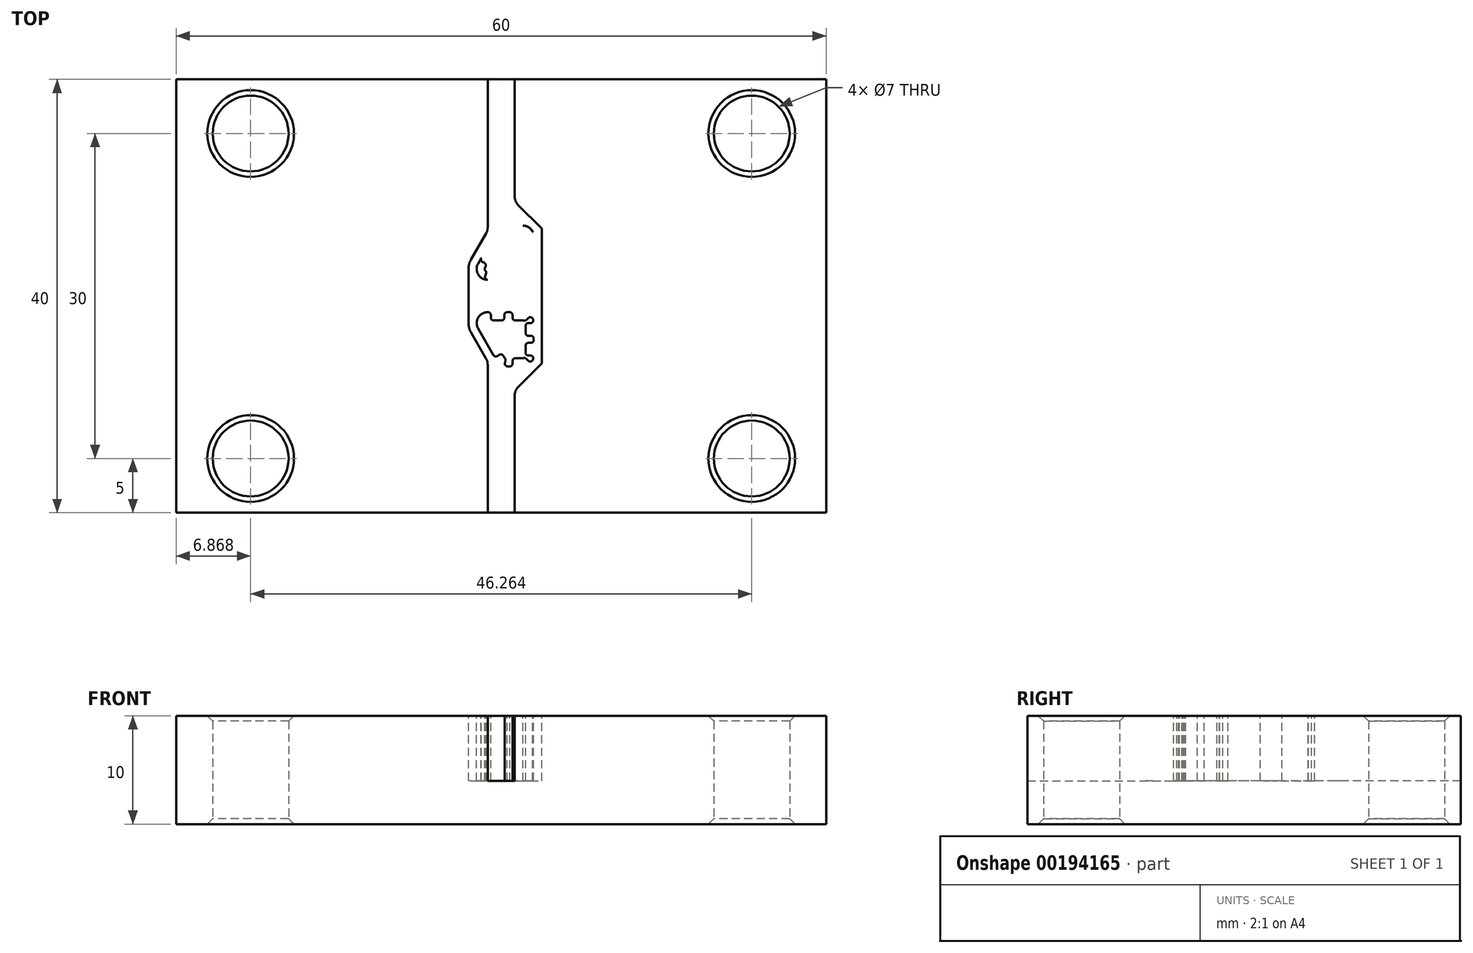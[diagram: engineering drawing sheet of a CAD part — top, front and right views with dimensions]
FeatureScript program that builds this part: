
annotation { "Feature Type Name" : "Feature", "Feature Type Description" : "" }
export const myFeature = defineFeature(function(context is Context, id is Id, definition is map)
    precondition{}
    {
        {
            var Q0;
            Q0=qCreatedBy(makeId("Top.planeOp"),FACE);
            var sketch = newSketch(context, id + "F0", { "sketchPlane" : qUnion([Q0])});
            skLineSegment(sketch, "E0.bottom", {"start": v(-30, 20) * mm, "end": v(30, 20) * mm});
            skLineSegment(sketch, "E0.top", {"start": v(-30, -20) * mm, "end": v(30, -20) * mm});
            skLineSegment(sketch, "E0.left", {"start": v(-30, 20) * mm, "end": v(-30, -20) * mm});
            skLineSegment(sketch, "E0.right", {"start": v(30, 20) * mm, "end": v(30, -20) * mm});
            skLineSegment(sketch, "E1", {"start": v(0, 99.86) * mm, "end": v(0, -61.69) * mm, "construction": true});
            skLineSegment(sketch, "E2", {"start": v(-65.53, 0) * mm, "end": v(113.19, 0) * mm, "construction": true});
            skLineSegment(sketch, "E3", {"start": v(-23.13, 86.06) * mm, "end": v(-23.13, -88.18) * mm, "construction": true});
            skLineSegment(sketch, "E4", {"start": v(23.13, 86.8) * mm, "end": v(23.13, -92.66) * mm, "construction": true});
            skLineSegment(sketch, "E5", {"start": v(-43.06, 15) * mm, "end": v(51.45, 15) * mm, "construction": true});
            skLineSegment(sketch, "E6", {"start": v(-43.93, -15) * mm, "end": v(58.43, -15) * mm, "construction": true});
            skCircle(sketch, "E7", {"center": v(-23.13, 15) * mm, "radius": 3.5 * mm});
            skCircle(sketch, "E8.MirrorC", {"center": v(23.13, 15) * mm, "radius": 3.5 * mm});
            skCircle(sketch, "E9.MirrorC", {"center": v(23.13, -15) * mm, "radius": 3.5 * mm});
            skCircle(sketch, "E10.MirrorC", {"center": v(-23.13, -15) * mm, "radius": 3.5 * mm});
            skSolve(sketch);
        }
        {
            var Q0;
            Q0=makeQuery(id+"F0.imprint","IMPRINT",FACE,{"disambiguationData":[TD([[makeQuery(id+"F0.imprint","IMPRINT",EDGE,{"derivedFrom":sQuery(id+"F0.wireOp",EDGE,"E0.bottom")}),-1.0]])]});
            extrude(context, id + "F1", {"entities" : qUnion([Q0]), "depth" : 10 * mm});
        }
        {
            var Q0;
            Q0=makeQuery(id+"F1.opExtrude","SWEPT_FACE",FACE,{"disambiguationData":[OSD([sQuery(id+"F0.wireOp",EDGE,"E7")])]});
            var Q1;
            Q1=makeQuery(id+"F1.opExtrude","SWEPT_FACE",FACE,{"disambiguationData":[OSD([sQuery(id+"F0.wireOp",EDGE,"E10.MirrorC")])]});
            var Q2;
            Q2=makeQuery(id+"F1.opExtrude","SWEPT_FACE",FACE,{"disambiguationData":[OSD([sQuery(id+"F0.wireOp",EDGE,"E9.MirrorC")])]});
            var Q3;
            Q3=makeQuery(id+"F1.opExtrude","SWEPT_FACE",FACE,{"disambiguationData":[OSD([sQuery(id+"F0.wireOp",EDGE,"E8.MirrorC")])]});
            chamfer(context, id + "F2", {"entities" : qUnion([Q0, Q1, Q2, Q3]), "width" : 0.5 * mm, "tangentPropagation" : true});
        }
        {
            var Q0;
            Q0=makeQuery(id+"F1.opExtrude","CAP_FACE",FACE,{"disambiguationData":[OSD([sQuery(id+"F0.wireOp",EDGE,"E0.bottom"),sQuery(id+"F0.wireOp",EDGE,"E0.top"),sQuery(id+"F0.wireOp",EDGE,"E0.left"),sQuery(id+"F0.wireOp",EDGE,"E0.right"),sQuery(id+"F0.wireOp",EDGE,"E7"),sQuery(id+"F0.wireOp",EDGE,"E8.MirrorC"),sQuery(id+"F0.wireOp",EDGE,"E9.MirrorC"),sQuery(id+"F0.wireOp",EDGE,"E10.MirrorC")])],"isStart":false});
            var sketch = newSketch(context, id + "F3", { "sketchPlane" : qUnion([Q0])});
            skLineSegment(sketch, "E11", {"start": v(0, 60.75) * mm, "end": v(0, -62.05) * mm, "construction": true});
            skLineSegment(sketch, "E12", {"start": v(-90.4, 0) * mm, "end": v(109.57, 0) * mm, "construction": true});
            skLineSegment(sketch, "E13", {"start": v(-1.27, 1.5) * mm, "end": v(2, 1.5) * mm});
            skLineSegment(sketch, "E14", {"start": v(3, 3.92) * mm, "end": v(3, 4.07) * mm});
            skLineSegment(sketch, "E15", {"start": v(2, 6.5) * mm, "end": v(0.46, 6.5) * mm});
            skLineSegment(sketch, "E16", {"start": v(-0.4, 6) * mm, "end": v(-2.13, 3) * mm});
            skArc(sketch, "E17", {"start": v(2.94, 5.83) * mm, "mid": v(2.58, 6.32) * mm, "end": v(2, 6.5) * mm});
            skArc(sketch, "E18", {"start": v(-2.13, 3) * mm, "mid": v(-2.13, 2) * mm, "end": v(-1.27, 1.5) * mm});
            skArc(sketch, "E19", {"start": v(0.46, 6.5) * mm, "mid": v(-0.04, 6.37) * mm, "end": v(-0.4, 6) * mm});
            skPoint(sketch, "E20.orphan", {"position": v(-3, 1.5) * mm});
            skLineSegment(sketch, "E21.trimOffspring", {"start": v(0, 6.5) * mm, "end": v(-0.11, 6.5) * mm});
            skLineSegment(sketch, "E22", {"start": v(2.7, 5.5) * mm, "end": v(2.5, 5.5) * mm});
            skLineSegment(sketch, "E23", {"start": v(2.25, 5.25) * mm, "end": v(2.25, 4.57) * mm});
            skLineSegment(sketch, "E24", {"start": v(2.5, 4.32) * mm, "end": v(2.75, 4.32) * mm});
            skArc(sketch, "E25", {"start": v(2.5, 5.5) * mm, "mid": v(2.32, 5.43) * mm, "end": v(2.25, 5.25) * mm});
            skLineSegment(sketch, "E26", {"start": v(2.17, 4.91) * mm, "end": v(3.34, 4.91) * mm, "construction": true});
            skPoint(sketch, "E26.startSnap0", {"position": v(2.25, 4.91) * mm});
            skArc(sketch, "E27.MirrorC", {"start": v(2.5, 4.32) * mm, "mid": v(2.32, 4.4) * mm, "end": v(2.25, 4.57) * mm});
            skArc(sketch, "E28", {"start": v(3, 4.07) * mm, "mid": v(2.93, 4.25) * mm, "end": v(2.75, 4.32) * mm});
            skArc(sketch, "E29", {"start": v(2.7, 5.5) * mm, "mid": v(2.91, 5.6) * mm, "end": v(2.94, 5.83) * mm});
            skPoint(sketch, "E30.orphan", {"position": v(3, 4.32) * mm});
            skPoint(sketch, "E31.orphan", {"position": v(3, 5.5) * mm});
            skPoint(sketch, "E32.orphan", {"position": v(2.25, 5.5) * mm});
            skPoint(sketch, "E33.orphan", {"position": v(2.25, 4.32) * mm});
            skLineSegment(sketch, "E34", {"start": v(1.75, 4) * mm, "end": v(4.02, 4) * mm, "construction": true});
            skArc(sketch, "E35.MirrorCS", {"start": v(2.7, 2.5) * mm, "mid": v(2.91, 2.4) * mm, "end": v(2.94, 2.17) * mm});
            skArc(sketch, "E36.MirrorCS", {"start": v(3, 3.92) * mm, "mid": v(2.93, 3.75) * mm, "end": v(2.75, 3.67) * mm});
            skArc(sketch, "E37.MirrorCS", {"start": v(2.5, 3.67) * mm, "mid": v(2.32, 3.6) * mm, "end": v(2.25, 3.42) * mm});
            skLineSegment(sketch, "E38.MirrorCS", {"start": v(2.5, 3.67) * mm, "end": v(2.75, 3.67) * mm});
            skPoint(sketch, "E39.MirrorP", {"position": v(2.25, 3.67) * mm});
            skArc(sketch, "E40.MirrorCS", {"start": v(2.5, 2.5) * mm, "mid": v(2.32, 2.57) * mm, "end": v(2.25, 2.75) * mm});
            skPoint(sketch, "E41.MirrorP", {"position": v(2.25, 3.09) * mm});
            skPoint(sketch, "E42.MirrorP", {"position": v(3, 3.67) * mm});
            skLineSegment(sketch, "E43.MirrorCS", {"start": v(2.25, 2.75) * mm, "end": v(2.25, 3.42) * mm});
            skLineSegment(sketch, "E44.MirrorCS", {"start": v(2.7, 2.5) * mm, "end": v(2.5, 2.5) * mm});
            skPoint(sketch, "E45.MirrorP", {"position": v(2.25, 2.5) * mm});
            skPoint(sketch, "E46.MirrorP", {"position": v(3, 2.5) * mm});
            skPoint(sketch, "E47.orphan", {"position": v(3, 8) * mm});
            skLineSegment(sketch, "E48", {"start": v(3.75, 20) * mm, "end": v(3.75, -20) * mm});
            skLineSegment(sketch, "E49", {"start": v(-3.02, 20) * mm, "end": v(-3.02, -20) * mm});
            skLineSegment(sketch, "E50", {"start": v(-1.25, 20) * mm, "end": v(-1.25, 6.3) * mm});
            skLineSegment(sketch, "E51", {"start": v(1.25, 20) * mm, "end": v(1.25, 9.14) * mm});
            skLineSegment(sketch, "E52", {"start": v(-2.78, 3.37) * mm, "end": v(-1.38, 5.8) * mm});
            skArc(sketch, "E53.trimOffspring", {"start": v(-2.78, 3.37) * mm, "mid": v(-2.96, 2.95) * mm, "end": v(-3.02, 2.5) * mm});
            skArc(sketch, "E54", {"start": v(-1.38, 5.8) * mm, "mid": v(-1.28, 6.04) * mm, "end": v(-1.25, 6.3) * mm});
            skLineSegment(sketch, "E55", {"start": v(1.54, 8.43) * mm, "end": v(3.75, 6.22) * mm});
            skArc(sketch, "E56", {"start": v(1.25, 9.14) * mm, "mid": v(1.33, 8.76) * mm, "end": v(1.54, 8.43) * mm});
            skCircle(sketch, "E57", {"center": v(2, 2.5) * mm, "radius": 1 * mm, "construction": true});
            skLineSegment(sketch, "E58", {"start": v(3, 6.49) * mm, "end": v(3, 1.28) * mm, "construction": true});
            skArc(sketch, "E59", {"start": v(2, 1.5) * mm, "mid": v(2.58, 1.68) * mm, "end": v(2.94, 2.17) * mm});
            skArc(sketch, "E60.MirrorCS", {"start": v(2.7, -5.5) * mm, "mid": v(2.91, -5.6) * mm, "end": v(2.94, -5.83) * mm});
            skLineSegment(sketch, "E61.MirrorCS", {"start": v(2.7, -5.5) * mm, "end": v(2.5, -5.5) * mm});
            skArc(sketch, "E62.MirrorCS", {"start": v(2.5, -5.5) * mm, "mid": v(2.32, -5.43) * mm, "end": v(2.25, -5.25) * mm});
            skArc(sketch, "E63.MirrorCS", {"start": v(3, -3.92) * mm, "mid": v(2.93, -3.75) * mm, "end": v(2.75, -3.67) * mm});
            skLineSegment(sketch, "E64.MirrorCS", {"start": v(2.5, -4.32) * mm, "end": v(2.75, -4.32) * mm});
            skLineSegment(sketch, "E65.MirrorCS", {"start": v(2.25, -5.25) * mm, "end": v(2.25, -4.57) * mm});
            skLineSegment(sketch, "E66.MirrorCS", {"start": v(3, -3.92) * mm, "end": v(3, -4.07) * mm});
            skArc(sketch, "E67.MirrorCS", {"start": v(2.5, -4.32) * mm, "mid": v(2.32, -4.4) * mm, "end": v(2.25, -4.57) * mm});
            skLineSegment(sketch, "E68.MirrorCS", {"start": v(2.17, -4.91) * mm, "end": v(3.34, -4.91) * mm, "construction": true});
            skArc(sketch, "E69.MirrorCS", {"start": v(3, -4.07) * mm, "mid": v(2.93, -4.25) * mm, "end": v(2.75, -4.32) * mm});
            skLineSegment(sketch, "E70.MirrorCS", {"start": v(2.5, -3.67) * mm, "end": v(2.75, -3.67) * mm});
            skArc(sketch, "E71.MirrorCS", {"start": v(2.5, -3.67) * mm, "mid": v(2.32, -3.6) * mm, "end": v(2.25, -3.42) * mm});
            skLineSegment(sketch, "E72.MirrorCS", {"start": v(2.7, -2.5) * mm, "end": v(2.5, -2.5) * mm});
            skLineSegment(sketch, "E73.MirrorCS", {"start": v(2.25, -2.75) * mm, "end": v(2.25, -3.42) * mm});
            skArc(sketch, "E74.MirrorCS", {"start": v(2.5, -2.5) * mm, "mid": v(2.32, -2.57) * mm, "end": v(2.25, -2.75) * mm});
            skArc(sketch, "E75.MirrorCS", {"start": v(2.7, -2.5) * mm, "mid": v(2.91, -2.4) * mm, "end": v(2.94, -2.17) * mm});
            skLineSegment(sketch, "E76.MirrorCS", {"start": v(0, -6.5) * mm, "end": v(-0.11, -6.5) * mm});
            skArc(sketch, "E77.MirrorCS", {"start": v(2.94, -5.83) * mm, "mid": v(2.58, -6.32) * mm, "end": v(2, -6.5) * mm});
            skArc(sketch, "E78.MirrorCS", {"start": v(1.25, -9.14) * mm, "mid": v(1.33, -8.76) * mm, "end": v(1.54, -8.43) * mm});
            skArc(sketch, "E79.MirrorCS", {"start": v(0.46, -6.5) * mm, "mid": v(-0.04, -6.37) * mm, "end": v(-0.4, -6) * mm});
            skLineSegment(sketch, "E80.MirrorCS", {"start": v(2, -6.5) * mm, "end": v(0.46, -6.5) * mm});
            skArc(sketch, "E81.MirrorCS", {"start": v(-1.38, -5.8) * mm, "mid": v(-1.28, -6.04) * mm, "end": v(-1.25, -6.3) * mm});
            skLineSegment(sketch, "E82.MirrorCS", {"start": v(3, -6.49) * mm, "end": v(3, -1.28) * mm, "construction": true});
            skLineSegment(sketch, "E83.MirrorCS", {"start": v(1.75, -4) * mm, "end": v(4.02, -4) * mm, "construction": true});
            skArc(sketch, "E84.MirrorCS", {"start": v(2, -1.5) * mm, "mid": v(2.58, -1.68) * mm, "end": v(2.94, -2.17) * mm});
            skPoint(sketch, "E85.MirrorP", {"position": v(3, -4.32) * mm});
            skPoint(sketch, "E86.MirrorP", {"position": v(2.25, -3.67) * mm});
            skLineSegment(sketch, "E87.MirrorCS", {"start": v(1.54, -8.43) * mm, "end": v(3.75, -6.22) * mm});
            skPoint(sketch, "E88.MirrorP", {"position": v(2.25, -4.32) * mm});
            skPoint(sketch, "E89.MirrorP", {"position": v(2.25, -4.91) * mm});
            skPoint(sketch, "E90.MirrorP", {"position": v(2.25, -5.5) * mm});
            skArc(sketch, "E91.MirrorCS", {"start": v(-2.78, -3.37) * mm, "mid": v(-2.96, -2.95) * mm, "end": v(-3.02, -2.5) * mm});
            skPoint(sketch, "E92.MirrorP", {"position": v(3, -5.5) * mm});
            skPoint(sketch, "E93.MirrorP", {"position": v(3, -3.67) * mm});
            skPoint(sketch, "E94.MirrorP", {"position": v(2.25, -3.09) * mm});
            skArc(sketch, "E95.MirrorCS", {"start": v(-2.13, -3) * mm, "mid": v(-2.13, -2) * mm, "end": v(-1.27, -1.5) * mm});
            skPoint(sketch, "E96.MirrorP", {"position": v(3, -2.5) * mm});
            skLineSegment(sketch, "E97.MirrorCS", {"start": v(-0.4, -6) * mm, "end": v(-2.13, -3) * mm});
            skLineSegment(sketch, "E98.MirrorCS", {"start": v(-1.27, -1.5) * mm, "end": v(2, -1.5) * mm});
            skPoint(sketch, "E99.MirrorP", {"position": v(2.25, -2.5) * mm});
            skPoint(sketch, "E100.MirrorP", {"position": v(-3, -1.5) * mm});
            skLineSegment(sketch, "E101.MirrorCS", {"start": v(-2.78, -3.37) * mm, "end": v(-1.38, -5.8) * mm});
            skLineSegment(sketch, "E102.MirrorCS", {"start": v(1.25, -20) * mm, "end": v(1.25, -9.14) * mm});
            skPoint(sketch, "E103.MirrorP", {"position": v(3, -8) * mm});
            skLineSegment(sketch, "E104.MirrorCS", {"start": v(-1.25, -20) * mm, "end": v(-1.25, -6.3) * mm});
            skCircle(sketch, "E105.MirrorC", {"center": v(2, -2.5) * mm, "radius": 1 * mm, "construction": true});
            skSolve(sketch);
        }
        {
            var Q0;
            Q0=makeQuery(id+"F3.imprint","IMPRINT",FACE,{"disambiguationData":[TD([[makeQuery(id+"F3.imprint","IMPRINT",EDGE,{"derivedFrom":sQuery(id+"F3.wireOp",EDGE,"E13")}),-1.0]])]});
            extrude(context, id + "F4", {"entities" : qUnion([Q0]), "operationType" : NewBodyOperationType.REMOVE, "oppositeDirection" : true, "depth" : 6 * mm});
        }
        {
            var Q0;
            Q0=makeQuery(id+"F4.boolean.opBoolean","SPLIT",FACE,{"disambiguationData":[TD([makeQuery(id+"F4.opExtrude","SWEPT_FACE",FACE,{"disambiguationData":[OSD([sQuery(id+"F3.wireOp",EDGE,"E13")])]})])],"derivedFrom":makeQuery(id+"F1.opExtrude","CAP_FACE",FACE,{"disambiguationData":[OSD([sQuery(id+"F0.wireOp",EDGE,"E0.bottom"),sQuery(id+"F0.wireOp",EDGE,"E0.top"),sQuery(id+"F0.wireOp",EDGE,"E0.left"),sQuery(id+"F0.wireOp",EDGE,"E0.right"),sQuery(id+"F0.wireOp",EDGE,"E7"),sQuery(id+"F0.wireOp",EDGE,"E8.MirrorC"),sQuery(id+"F0.wireOp",EDGE,"E9.MirrorC"),sQuery(id+"F0.wireOp",EDGE,"E10.MirrorC")])],"isStart":false})});
            var sketch = newSketch(context, id + "F5", { "sketchPlane" : qUnion([Q0])});
            skLineSegment(sketch, "E106", {"start": v(2.25, 5.48) * mm, "end": v(2.25, 2.5) * mm, "construction": true});
            skPoint(sketch, "E106.startSnap0", {"position": v(2.25, 4.91) * mm});
            skPoint(sketch, "E107.startSnap0", {"position": v(2.91, 2.4) * mm});
            skLineSegment(sketch, "E108", {"start": v(-1.48, 2.62) * mm, "end": v(0.25, 5.62) * mm, "construction": true});
            skLineSegment(sketch, "E109", {"start": v(0.46, 5.75) * mm, "end": v(1.98, 5.75) * mm, "construction": true});
            skLineSegment(sketch, "E110", {"start": v(-1.27, 2.25) * mm, "end": v(2, 2.25) * mm, "construction": true});
            skPoint(sketch, "E111.orphan", {"position": v(2.25, 6.5) * mm});
            skArc(sketch, "E112", {"start": v(-1.48, 2.62) * mm, "mid": v(-1.48, 2.37) * mm, "end": v(-1.27, 2.25) * mm, "construction": true});
            skArc(sketch, "E113", {"start": v(0.46, 5.75) * mm, "mid": v(0.34, 5.72) * mm, "end": v(0.25, 5.62) * mm, "construction": true});
            skArc(sketch, "E114", {"start": v(2.25, 5.48) * mm, "mid": v(2.17, 5.67) * mm, "end": v(1.98, 5.75) * mm, "construction": true});
            skArc(sketch, "E115", {"start": v(2, 2.25) * mm, "mid": v(2.18, 2.32) * mm, "end": v(2.25, 2.5) * mm, "construction": true});
            skPoint(sketch, "E116.orphan", {"position": v(2.7, 6.2) * mm});
            skPoint(sketch, "E117.orphan", {"position": v(-0.04, 6.37) * mm});
            skLineSegment(sketch, "E118", {"start": v(3.45, 5.5) * mm, "end": v(1.72, 5.5) * mm, "construction": true});
            skLineSegment(sketch, "E119", {"start": v(2, 6.65) * mm, "end": v(2, 5.2) * mm, "construction": true});
            skArc(sketch, "E120", {"start": v(2, 6.5) * mm, "mid": v(2.7, 6.2) * mm, "end": v(3, 5.5) * mm});
            skLineSegment(sketch, "E121", {"start": v(2, 5.5) * mm, "end": v(2.88, 6.32) * mm, "construction": true});
            skArc(sketch, "E122", {"start": v(2.92, 5.9) * mm, "mid": v(2.74, 6.04) * mm, "end": v(2.52, 5.98) * mm});
            skArc(sketch, "E123", {"start": v(2.07, 5.74) * mm, "mid": v(2.2, 5.73) * mm, "end": v(2.31, 5.8) * mm});
            skArc(sketch, "E124", {"start": v(1.04, 6) * mm, "mid": v(1.11, 5.82) * mm, "end": v(1.3, 5.75) * mm});
            skArc(sketch, "E125", {"start": v(1.04, 6.25) * mm, "mid": v(0.97, 6.43) * mm, "end": v(0.8, 6.5) * mm});
            skLineSegment(sketch, "E126", {"start": v(1.04, 6.25) * mm, "end": v(1.04, 6) * mm});
            skLineSegment(sketch, "E127.trimOffspring", {"start": v(1.04, 6.25) * mm, "end": v(1.04, 6) * mm, "construction": true});
            skLineSegment(sketch, "E128", {"start": v(2, 2.5) * mm, "end": v(3.17, 1.41) * mm, "construction": true});
            skArc(sketch, "E129", {"start": v(2.52, 2.02) * mm, "mid": v(2.74, 1.96) * mm, "end": v(2.92, 2.1) * mm});
            skArc(sketch, "E130", {"start": v(2.32, 2.2) * mm, "mid": v(2.2, 2.27) * mm, "end": v(2.07, 2.26) * mm});
            skLineSegment(sketch, "E131", {"start": v(2.48, 1.97) * mm, "end": v(2.52, 2.02) * mm, "construction": true});
            skLineSegment(sketch, "E132", {"start": v(2.32, 2.2) * mm, "end": v(2.52, 2.02) * mm});
            skLineSegment(sketch, "E133", {"start": v(1.04, 2.32) * mm, "end": v(1.04, 1.29) * mm, "construction": true});
            skLineSegment(sketch, "E134", {"start": v(2, 2.25) * mm, "end": v(2, 1.38) * mm, "construction": true});
            skArc(sketch, "E135", {"start": v(1.3, 2.25) * mm, "mid": v(1.11, 2.18) * mm, "end": v(1.04, 2) * mm});
            skArc(sketch, "E136", {"start": v(0.8, 1.5) * mm, "mid": v(0.97, 1.57) * mm, "end": v(1.04, 1.75) * mm});
            skLineSegment(sketch, "E137", {"start": v(1.3, 2.25) * mm, "end": v(2, 2.25) * mm});
            skArc(sketch, "E138", {"start": v(2.07, 2.26) * mm, "mid": v(2.04, 2.25) * mm, "end": v(2, 2.25) * mm});
            skLineSegment(sketch, "E139", {"start": v(0.8, 1.75) * mm, "end": v(1.08, 1.75) * mm, "construction": true});
            skLineSegment(sketch, "E140", {"start": v(0.8, 2.02) * mm, "end": v(0.8, 1.42) * mm, "construction": true});
            skLineSegment(sketch, "E141", {"start": v(1.04, 2) * mm, "end": v(1.04, 1.75) * mm});
            skLineSegment(sketch, "E142", {"start": v(0.3, 2) * mm, "end": v(0.3, 1.75) * mm});
            skArc(sketch, "E143", {"start": v(0.3, 1.75) * mm, "mid": v(0.36, 1.57) * mm, "end": v(0.54, 1.5) * mm});
            skArc(sketch, "E144", {"start": v(0.3, 2) * mm, "mid": v(0.22, 2.18) * mm, "end": v(0.04, 2.25) * mm});
            skPoint(sketch, "E145.orphan", {"position": v(0.5, 1.75) * mm});
            skLineSegment(sketch, "E146", {"start": v(0.54, 1.77) * mm, "end": v(0.54, 1.46) * mm, "construction": true});
            skLineSegment(sketch, "E147", {"start": v(-0.96, 2.45) * mm, "end": v(-0.96, 1.28) * mm, "construction": true});
            skLineSegment(sketch, "E148", {"start": v(-0.96, 2) * mm, "end": v(-0.96, 1.75) * mm});
            skLineSegment(sketch, "E149", {"start": v(-0.33, 2.42) * mm, "end": v(-0.33, 1.38) * mm, "construction": true});
            skArc(sketch, "E150.MirrorCS", {"start": v(-0.96, 2) * mm, "mid": v(-0.89, 2.18) * mm, "end": v(-0.7, 2.25) * mm});
            skArc(sketch, "E151.MirrorCS", {"start": v(-0.96, 1.75) * mm, "mid": v(-1.03, 1.57) * mm, "end": v(-1.2, 1.5) * mm});
            skLineSegment(sketch, "E152", {"start": v(-0.7, 2.25) * mm, "end": v(0.04, 2.25) * mm});
            skLineSegment(sketch, "E153", {"start": v(0.46, 5.75) * mm, "end": v(0.46, 6.64) * mm, "construction": true});
            skLineSegment(sketch, "E154", {"start": v(0.46, 5.5) * mm, "end": v(0.23, 6.83) * mm, "construction": true});
            skArc(sketch, "E155", {"start": v(0.59, 6.5) * mm, "mid": v(0.4, 6.41) * mm, "end": v(0.34, 6.2) * mm});
            skArc(sketch, "E156", {"start": v(0.3, 5.7) * mm, "mid": v(0.38, 5.8) * mm, "end": v(0.39, 5.93) * mm});
            skLineSegment(sketch, "E157", {"start": v(0.59, 6.2) * mm, "end": v(0.59, 6.67) * mm, "construction": true});
            skLineSegment(sketch, "E158", {"start": v(0.39, 5.93) * mm, "end": v(0.34, 6.2) * mm});
            skLineSegment(sketch, "E159", {"start": v(0.33, 5.58) * mm, "end": v(-0.79, 6.22) * mm, "construction": true});
            skLineSegment(sketch, "E160", {"start": v(-0.38, 5.55) * mm, "end": v(-0.16, 5.42) * mm});
            skArc(sketch, "E161", {"start": v(-0.16, 5.42) * mm, "mid": v(0.03, 5.4) * mm, "end": v(0.18, 5.51) * mm});
            skArc(sketch, "E162", {"start": v(-0.38, 5.55) * mm, "mid": v(-0.57, 5.57) * mm, "end": v(-0.72, 5.45) * mm});
            skLineSegment(sketch, "E163.trimOffspring", {"start": v(0.06, 5.3) * mm, "end": v(0.33, 5.14) * mm});
            skLineSegment(sketch, "E164", {"start": v(-0.82, 5.51) * mm, "end": v(-0.5, 5.33) * mm, "construction": true});
            skLineSegment(sketch, "E165", {"start": v(-0.5, 5.33) * mm, "end": v(-0.38, 5.55) * mm, "construction": true});
            skLineSegment(sketch, "E166", {"start": v(-0.75, 4.9) * mm, "end": v(-0.53, 4.77) * mm});
            skArc(sketch, "E167", {"start": v(-0.84, 5.24) * mm, "mid": v(-0.87, 5.05) * mm, "end": v(-0.75, 4.9) * mm});
            skArc(sketch, "E168", {"start": v(-0.44, 4.43) * mm, "mid": v(-0.42, 4.62) * mm, "end": v(-0.53, 4.77) * mm});
            skLineSegment(sketch, "E169", {"start": v(-0.63, 5.11) * mm, "end": v(-0.9, 5.28) * mm, "construction": true});
            skLineSegment(sketch, "E170", {"start": v(-0.63, 4.1) * mm, "end": v(-1.44, 4.57) * mm, "construction": true});
            skArc(sketch, "E171.MirrorCS", {"start": v(-0.82, 3.78) * mm, "mid": v(-0.97, 3.66) * mm, "end": v(-1.16, 3.69) * mm});
            skLineSegment(sketch, "E172.MirrorCS", {"start": v(-1.38, 3.81) * mm, "end": v(-1.16, 3.69) * mm});
            skArc(sketch, "E173.MirrorCS", {"start": v(-1.72, 3.72) * mm, "mid": v(-1.57, 3.84) * mm, "end": v(-1.38, 3.81) * mm});
            skArc(sketch, "E174.MirrorCS", {"start": v(-1.75, 3.16) * mm, "mid": v(-1.87, 3.32) * mm, "end": v(-1.84, 3.5) * mm});
            skLineSegment(sketch, "E175.MirrorCS", {"start": v(-1.75, 3.16) * mm, "end": v(-1.53, 3.04) * mm});
            skArc(sketch, "E176.MirrorCS", {"start": v(-1.53, 3.04) * mm, "mid": v(-1.42, 2.89) * mm, "end": v(-1.44, 2.7) * mm});
            skLineSegment(sketch, "E177", {"start": v(-1.84, 3.5) * mm, "end": v(-1.72, 3.72) * mm});
            skLineSegment(sketch, "E178", {"start": v(-0.84, 5.24) * mm, "end": v(-0.72, 5.45) * mm});
            skLineSegment(sketch, "E179", {"start": v(0.18, 5.51) * mm, "end": v(0.25, 5.62) * mm});
            skLineSegment(sketch, "E180", {"start": v(-0.82, 3.78) * mm, "end": v(-0.44, 4.43) * mm});
            skArc(sketch, "E181", {"start": v(0.25, 5.62) * mm, "mid": v(0.27, 5.66) * mm, "end": v(0.3, 5.7) * mm});
            skLineSegment(sketch, "E182", {"start": v(-1.27, 2.5) * mm, "end": v(-1.62, 1.4) * mm, "construction": true});
            skArc(sketch, "E183", {"start": v(-1.49, 1.83) * mm, "mid": v(-1.45, 1.6) * mm, "end": v(-1.25, 1.5) * mm});
            skArc(sketch, "E184", {"start": v(-1.4, 2.09) * mm, "mid": v(-1.4, 2.22) * mm, "end": v(-1.45, 2.33) * mm});
            skLineSegment(sketch, "E185", {"start": v(-1.25, 1.5) * mm, "end": v(-1.2, 1.5) * mm});
            skLineSegment(sketch, "E186", {"start": v(-1.49, 1.83) * mm, "end": v(-1.4, 2.09) * mm});
            skArc(sketch, "E187", {"start": v(-1.45, 2.33) * mm, "mid": v(-1.52, 2.47) * mm, "end": v(-1.48, 2.62) * mm});
            skLineSegment(sketch, "E188", {"start": v(-1.48, 2.62) * mm, "end": v(-1.44, 2.7) * mm});
            skLineSegment(sketch, "E189", {"start": v(1.3, 5.75) * mm, "end": v(1.98, 5.75) * mm});
            skArc(sketch, "E190", {"start": v(1.98, 5.75) * mm, "mid": v(2.03, 5.75) * mm, "end": v(2.07, 5.74) * mm});
            skLineSegment(sketch, "E191", {"start": v(-5.65, 0) * mm, "end": v(4.56, 0) * mm, "construction": true});
            skArc(sketch, "E192", {"start": v(-2.13, 3) * mm, "mid": v(-2.13, 2) * mm, "end": v(-1.27, 1.5) * mm});
            skLineSegment(sketch, "E193", {"start": v(-2.13, 3) * mm, "end": v(-0.4, 6) * mm});
            skArc(sketch, "E194", {"start": v(-0.4, 6) * mm, "mid": v(-0.04, 6.37) * mm, "end": v(0.46, 6.5) * mm});
            skLineSegment(sketch, "E195", {"start": v(0.46, 6.5) * mm, "end": v(2, 6.5) * mm});
            skArc(sketch, "E196", {"start": v(2, 6.5) * mm, "mid": v(2.55, 6.33) * mm, "end": v(2.92, 5.89) * mm});
            skLineSegment(sketch, "E197", {"start": v(-1.25, 1.5) * mm, "end": v(2, 1.5) * mm});
            skArc(sketch, "E198", {"start": v(2, 1.5) * mm, "mid": v(2.55, 1.66) * mm, "end": v(2.92, 2.1) * mm});
            skLineSegment(sketch, "E199", {"start": v(2.31, 5.8) * mm, "end": v(2.52, 5.98) * mm});
            skArc(sketch, "E200.MirrorCS", {"start": v(2.07, -2.26) * mm, "mid": v(2.04, -2.25) * mm, "end": v(2, -2.25) * mm});
            skArc(sketch, "E201.MirrorCS", {"start": v(1.98, -5.75) * mm, "mid": v(2.03, -5.75) * mm, "end": v(2.07, -5.74) * mm});
            skArc(sketch, "E202.MirrorCS", {"start": v(2.25, -5.48) * mm, "mid": v(2.17, -5.67) * mm, "end": v(1.98, -5.75) * mm, "construction": true});
            skArc(sketch, "E203.MirrorCS", {"start": v(2, -2.25) * mm, "mid": v(2.18, -2.32) * mm, "end": v(2.25, -2.5) * mm, "construction": true});
            skArc(sketch, "E204.MirrorCS", {"start": v(2.32, -2.2) * mm, "mid": v(2.2, -2.27) * mm, "end": v(2.07, -2.26) * mm});
            skArc(sketch, "E205.MirrorCS", {"start": v(2.07, -5.74) * mm, "mid": v(2.2, -5.73) * mm, "end": v(2.31, -5.8) * mm});
            skArc(sketch, "E206.MirrorCS", {"start": v(0.25, -5.62) * mm, "mid": v(0.27, -5.66) * mm, "end": v(0.3, -5.7) * mm});
            skLineSegment(sketch, "E207.MirrorCS", {"start": v(-0.96, -2) * mm, "end": v(-0.96, -1.75) * mm});
            skArc(sketch, "E208.MirrorCS", {"start": v(-0.96, -1.75) * mm, "mid": v(-1.03, -1.57) * mm, "end": v(-1.2, -1.5) * mm});
            skArc(sketch, "E209.MirrorCS", {"start": v(-1.49, -1.83) * mm, "mid": v(-1.45, -1.6) * mm, "end": v(-1.25, -1.5) * mm});
            skLineSegment(sketch, "E210.MirrorCS", {"start": v(-1.25, -1.5) * mm, "end": v(-1.2, -1.5) * mm});
            skArc(sketch, "E211.MirrorCS", {"start": v(-1.45, -2.33) * mm, "mid": v(-1.52, -2.47) * mm, "end": v(-1.48, -2.62) * mm});
            skArc(sketch, "E212.MirrorCS", {"start": v(-1.48, -2.62) * mm, "mid": v(-1.48, -2.37) * mm, "end": v(-1.27, -2.25) * mm, "construction": true});
            skArc(sketch, "E213.MirrorCS", {"start": v(0.46, -5.75) * mm, "mid": v(0.34, -5.72) * mm, "end": v(0.25, -5.62) * mm, "construction": true});
            skArc(sketch, "E214.MirrorCS", {"start": v(-0.96, -2) * mm, "mid": v(-0.89, -2.18) * mm, "end": v(-0.7, -2.25) * mm});
            skLineSegment(sketch, "E215.MirrorCS", {"start": v(2.32, -2.2) * mm, "end": v(2.52, -2.02) * mm});
            skArc(sketch, "E216.MirrorCS", {"start": v(0.8, -1.5) * mm, "mid": v(0.97, -1.57) * mm, "end": v(1.04, -1.75) * mm});
            skArc(sketch, "E217.MirrorCS", {"start": v(-1.4, -2.09) * mm, "mid": v(-1.4, -2.22) * mm, "end": v(-1.45, -2.33) * mm});
            skLineSegment(sketch, "E218.MirrorCS", {"start": v(0.8, -1.75) * mm, "end": v(1.08, -1.75) * mm, "construction": true});
            skLineSegment(sketch, "E219.MirrorCS", {"start": v(-1.49, -1.83) * mm, "end": v(-1.4, -2.09) * mm});
            skLineSegment(sketch, "E220.MirrorCS", {"start": v(-1.48, -2.62) * mm, "end": v(-1.44, -2.7) * mm});
            skArc(sketch, "E221.MirrorCS", {"start": v(0.3, -5.7) * mm, "mid": v(0.38, -5.8) * mm, "end": v(0.39, -5.93) * mm});
            skLineSegment(sketch, "E222.MirrorCS", {"start": v(0.8, -2.02) * mm, "end": v(0.8, -1.42) * mm, "construction": true});
            skLineSegment(sketch, "E223.MirrorCS", {"start": v(-0.96, -2.45) * mm, "end": v(-0.96, -1.28) * mm, "construction": true});
            skLineSegment(sketch, "E224.MirrorCS", {"start": v(0.18, -5.51) * mm, "end": v(0.25, -5.62) * mm});
            skLineSegment(sketch, "E225.MirrorCS", {"start": v(0.06, -5.3) * mm, "end": v(0.33, -5.14) * mm});
            skLineSegment(sketch, "E226.MirrorCS", {"start": v(0.54, -1.77) * mm, "end": v(0.54, -1.46) * mm, "construction": true});
            skLineSegment(sketch, "E227.MirrorCS", {"start": v(1.04, -2) * mm, "end": v(1.04, -1.75) * mm});
            skLineSegment(sketch, "E228.MirrorCS", {"start": v(1.04, -6.25) * mm, "end": v(1.04, -6) * mm});
            skLineSegment(sketch, "E229.MirrorCS", {"start": v(0.3, -2) * mm, "end": v(0.3, -1.75) * mm});
            skArc(sketch, "E230.MirrorCS", {"start": v(0.3, -1.75) * mm, "mid": v(0.36, -1.57) * mm, "end": v(0.54, -1.5) * mm});
            skLineSegment(sketch, "E231.MirrorCS", {"start": v(2.48, -1.97) * mm, "end": v(2.52, -2.02) * mm, "construction": true});
            skLineSegment(sketch, "E232.MirrorCS", {"start": v(-0.5, -5.33) * mm, "end": v(-0.38, -5.55) * mm, "construction": true});
            skLineSegment(sketch, "E233.MirrorCS", {"start": v(-0.82, -5.51) * mm, "end": v(-0.5, -5.33) * mm, "construction": true});
            skArc(sketch, "E234.MirrorCS", {"start": v(-0.84, -5.24) * mm, "mid": v(-0.87, -5.05) * mm, "end": v(-0.75, -4.9) * mm});
            skArc(sketch, "E235.MirrorCS", {"start": v(1.3, -2.25) * mm, "mid": v(1.11, -2.18) * mm, "end": v(1.04, -2) * mm});
            skLineSegment(sketch, "E236.MirrorCS", {"start": v(2.31, -5.8) * mm, "end": v(2.52, -5.98) * mm});
            skLineSegment(sketch, "E237.MirrorCS", {"start": v(-0.7, -2.25) * mm, "end": v(0.04, -2.25) * mm});
            skLineSegment(sketch, "E238.MirrorCS", {"start": v(-0.63, -5.11) * mm, "end": v(-0.9, -5.28) * mm, "construction": true});
            skLineSegment(sketch, "E239.MirrorCS", {"start": v(1.3, -2.25) * mm, "end": v(2, -2.25) * mm});
            skArc(sketch, "E240.MirrorCS", {"start": v(0.59, -6.5) * mm, "mid": v(0.4, -6.41) * mm, "end": v(0.34, -6.2) * mm});
            skArc(sketch, "E241.MirrorCS", {"start": v(-1.53, -3.04) * mm, "mid": v(-1.42, -2.89) * mm, "end": v(-1.44, -2.7) * mm});
            skLineSegment(sketch, "E242.MirrorCS", {"start": v(-0.38, -5.55) * mm, "end": v(-0.16, -5.42) * mm});
            skArc(sketch, "E243.MirrorCS", {"start": v(-0.16, -5.42) * mm, "mid": v(0.03, -5.4) * mm, "end": v(0.18, -5.51) * mm});
            skLineSegment(sketch, "E244.MirrorCS", {"start": v(-0.84, -5.24) * mm, "end": v(-0.72, -5.45) * mm});
            skArc(sketch, "E245.MirrorCS", {"start": v(-0.38, -5.55) * mm, "mid": v(-0.57, -5.57) * mm, "end": v(-0.72, -5.45) * mm});
            skLineSegment(sketch, "E246.MirrorCS", {"start": v(1.04, -6.25) * mm, "end": v(1.04, -6) * mm, "construction": true});
            skArc(sketch, "E247.MirrorCS", {"start": v(-1.75, -3.16) * mm, "mid": v(-1.87, -3.32) * mm, "end": v(-1.84, -3.5) * mm});
            skLineSegment(sketch, "E248.MirrorCS", {"start": v(0.39, -5.93) * mm, "end": v(0.34, -6.2) * mm});
            skLineSegment(sketch, "E249.MirrorCS", {"start": v(-1.75, -3.16) * mm, "end": v(-1.53, -3.04) * mm});
            skArc(sketch, "E250.MirrorCS", {"start": v(1.04, -6.25) * mm, "mid": v(0.97, -6.43) * mm, "end": v(0.8, -6.5) * mm});
            skLineSegment(sketch, "E251.MirrorCS", {"start": v(2, -6.65) * mm, "end": v(2, -5.2) * mm, "construction": true});
            skLineSegment(sketch, "E252.MirrorCS", {"start": v(2, -5.5) * mm, "end": v(2.88, -6.32) * mm, "construction": true});
            skArc(sketch, "E253.MirrorCS", {"start": v(2.92, -5.9) * mm, "mid": v(2.74, -6.04) * mm, "end": v(2.52, -5.98) * mm});
            skLineSegment(sketch, "E254.MirrorCS", {"start": v(-0.75, -4.9) * mm, "end": v(-0.53, -4.77) * mm});
            skLineSegment(sketch, "E255.MirrorCS", {"start": v(2, -2.25) * mm, "end": v(2, -1.38) * mm, "construction": true});
            skLineSegment(sketch, "E256.MirrorCS", {"start": v(0.46, -5.75) * mm, "end": v(0.46, -6.64) * mm, "construction": true});
            skArc(sketch, "E257.MirrorCS", {"start": v(-0.82, -3.78) * mm, "mid": v(-0.97, -3.66) * mm, "end": v(-1.16, -3.69) * mm});
            skLineSegment(sketch, "E258.MirrorCS", {"start": v(0.46, -5.5) * mm, "end": v(0.23, -6.83) * mm, "construction": true});
            skLineSegment(sketch, "E259.MirrorCS", {"start": v(-1.38, -3.81) * mm, "end": v(-1.16, -3.69) * mm});
            skArc(sketch, "E260.MirrorCS", {"start": v(0.3, -2) * mm, "mid": v(0.22, -2.18) * mm, "end": v(0.04, -2.25) * mm});
            skLineSegment(sketch, "E261.MirrorCS", {"start": v(-1.84, -3.5) * mm, "end": v(-1.72, -3.72) * mm});
            skLineSegment(sketch, "E262.MirrorCS", {"start": v(1.3, -5.75) * mm, "end": v(1.98, -5.75) * mm});
            skArc(sketch, "E263.MirrorCS", {"start": v(-1.72, -3.72) * mm, "mid": v(-1.57, -3.84) * mm, "end": v(-1.38, -3.81) * mm});
            skArc(sketch, "E264.MirrorCS", {"start": v(2.52, -2.02) * mm, "mid": v(2.74, -1.96) * mm, "end": v(2.92, -2.1) * mm});
            skLineSegment(sketch, "E265.MirrorCS", {"start": v(0.59, -6.2) * mm, "end": v(0.59, -6.67) * mm, "construction": true});
            skArc(sketch, "E266.MirrorCS", {"start": v(1.04, -6) * mm, "mid": v(1.11, -5.82) * mm, "end": v(1.3, -5.75) * mm});
            skLineSegment(sketch, "E267.MirrorCS", {"start": v(-1.27, -2.25) * mm, "end": v(2, -2.25) * mm, "construction": true});
            skLineSegment(sketch, "E268.MirrorCS", {"start": v(1.04, -2.32) * mm, "end": v(1.04, -1.29) * mm, "construction": true});
            skArc(sketch, "E269.MirrorCS", {"start": v(2, -6.5) * mm, "mid": v(2.55, -6.33) * mm, "end": v(2.92, -5.89) * mm});
            skLineSegment(sketch, "E270.MirrorCS", {"start": v(-0.82, -3.78) * mm, "end": v(-0.44, -4.43) * mm});
            skLineSegment(sketch, "E271.MirrorCS", {"start": v(-0.33, -2.42) * mm, "end": v(-0.33, -1.38) * mm, "construction": true});
            skArc(sketch, "E272.MirrorCS", {"start": v(-0.44, -4.43) * mm, "mid": v(-0.42, -4.62) * mm, "end": v(-0.53, -4.77) * mm});
            skLineSegment(sketch, "E273.MirrorCS", {"start": v(3.45, -5.5) * mm, "end": v(1.72, -5.5) * mm, "construction": true});
            skArc(sketch, "E274.MirrorCS", {"start": v(2, -6.5) * mm, "mid": v(2.7, -6.2) * mm, "end": v(3, -5.5) * mm});
            skLineSegment(sketch, "E275.MirrorCS", {"start": v(-1.25, -1.5) * mm, "end": v(2, -1.5) * mm});
            skArc(sketch, "E276.MirrorCS", {"start": v(2, -1.5) * mm, "mid": v(2.55, -1.66) * mm, "end": v(2.92, -2.1) * mm});
            skLineSegment(sketch, "E277.MirrorCS", {"start": v(-1.27, -2.5) * mm, "end": v(-1.62, -1.4) * mm, "construction": true});
            skPoint(sketch, "E278.MirrorP", {"position": v(0.5, -1.75) * mm});
            skPoint(sketch, "E279.MirrorP", {"position": v(2.7, -6.2) * mm});
            skLineSegment(sketch, "E280.MirrorCS", {"start": v(2, -2.5) * mm, "end": v(3.17, -1.41) * mm, "construction": true});
            skLineSegment(sketch, "E281.MirrorCS", {"start": v(0.33, -5.58) * mm, "end": v(-0.79, -6.22) * mm, "construction": true});
            skLineSegment(sketch, "E282.MirrorCS", {"start": v(-1.48, -2.62) * mm, "end": v(0.25, -5.62) * mm, "construction": true});
            skLineSegment(sketch, "E283.MirrorCS", {"start": v(-2.13, -3) * mm, "end": v(-0.4, -6) * mm});
            skArc(sketch, "E284.MirrorCS", {"start": v(-0.4, -6) * mm, "mid": v(-0.04, -6.37) * mm, "end": v(0.46, -6.5) * mm});
            skPoint(sketch, "E285.MirrorP", {"position": v(2.91, -2.4) * mm});
            skLineSegment(sketch, "E286.MirrorCS", {"start": v(0.46, -6.5) * mm, "end": v(2, -6.5) * mm});
            skLineSegment(sketch, "E287.MirrorCS", {"start": v(0.46, -5.75) * mm, "end": v(1.98, -5.75) * mm, "construction": true});
            skPoint(sketch, "E288.MirrorP", {"position": v(2.25, -6.5) * mm});
            skLineSegment(sketch, "E289.MirrorCS", {"start": v(2.25, -5.48) * mm, "end": v(2.25, -2.5) * mm, "construction": true});
            skLineSegment(sketch, "E290.MirrorCS", {"start": v(-0.63, -4.1) * mm, "end": v(-1.44, -4.57) * mm, "construction": true});
            skArc(sketch, "E291.MirrorCS", {"start": v(-2.13, -3) * mm, "mid": v(-2.13, -2) * mm, "end": v(-1.27, -1.5) * mm});
            skPoint(sketch, "E292.MirrorP", {"position": v(-0.04, -6.37) * mm});
            skPoint(sketch, "E293.MirrorP", {"position": v(2.25, -4.91) * mm});
            skLineSegment(sketch, "E294", {"start": v(-1.27, -1.5) * mm, "end": v(-1.2, -1.5) * mm});
            skSolve(sketch);
        }
        {
            var Q0;
            {var subQ2=sQuery(id+"F5.wireOp",EDGE,"E174.MirrorCS");Q0=makeQuery(id+"F5.imprint","IMPRINT",FACE,{"disambiguationData":[TD([[makeQuery(id+"F5.imprint","IMPRINT",EDGE,{"derivedFrom":subQ2}),1.0]])]});}
            var Q1;
            Q1=makeQuery(id+"F5.imprint","IMPRINT",FACE,{"disambiguationData":[TD([[makeQuery(id+"F5.imprint","IMPRINT",EDGE,{"derivedFrom":sQuery(id+"F5.wireOp",EDGE,"E166")}),-1.0]])]});
            var Q2;
            {var subQ4=sQuery(id+"F5.wireOp",EDGE,"E155");Q2=makeQuery(id+"F5.imprint","IMPRINT",FACE,{"disambiguationData":[TD([[makeQuery(id+"F5.imprint","IMPRINT",EDGE,{"derivedFrom":subQ4}),-1.0]])]});}
            var Q3;
            Q3=makeQuery(id+"F5.imprint","IMPRINT",FACE,{"disambiguationData":[TD([[makeQuery(id+"F5.imprint","IMPRINT",EDGE,{"derivedFrom":sQuery(id+"F5.wireOp",EDGE,"E123")}),1.0]])]});
            var Q4;
            Q4=makeQuery(id+"F5.imprint","IMPRINT",FACE,{"disambiguationData":[TD([[makeQuery(id+"F5.imprint","IMPRINT",EDGE,{"derivedFrom":sQuery(id+"F5.wireOp",EDGE,"E130")}),1.0]])]});
            var Q5;
            {var subQ5=sQuery(id+"F5.wireOp",EDGE,"E142");Q5=makeQuery(id+"F5.imprint","IMPRINT",FACE,{"disambiguationData":[TD([[makeQuery(id+"F5.imprint","IMPRINT",EDGE,{"derivedFrom":subQ5}),-1.0]])]});}
            var Q6;
            Q6=makeQuery(id+"F5.imprint","IMPRINT",FACE,{"disambiguationData":[TD([[makeQuery(id+"F5.imprint","IMPRINT",EDGE,{"derivedFrom":sQuery(id+"F5.wireOp",EDGE,"E200.MirrorCS")}),-1.0]])]});
            var Q7;
            Q7=makeQuery(id+"F5.imprint","IMPRINT",FACE,{"disambiguationData":[TD([[makeQuery(id+"F5.imprint","IMPRINT",EDGE,{"derivedFrom":sQuery(id+"F5.wireOp",EDGE,"E214.MirrorCS")}),1.0]])]});
            var Q8;
            {var subQ0=sQuery(id+"F5.wireOp",EDGE,"E234.MirrorCS");Q8=makeQuery(id+"F5.imprint","IMPRINT",FACE,{"disambiguationData":[TD([[makeQuery(id+"F5.imprint","IMPRINT",EDGE,{"derivedFrom":subQ0}),1.0]])]});}
            var Q9;
            Q9=makeQuery(id+"F5.imprint","IMPRINT",FACE,{"disambiguationData":[TD([[makeQuery(id+"F5.imprint","IMPRINT",EDGE,{"derivedFrom":sQuery(id+"F5.wireOp",EDGE,"E206.MirrorCS")}),-1.0]])]});
            var Q10;
            Q10=makeQuery(id+"F5.imprint","IMPRINT",FACE,{"disambiguationData":[TD([[makeQuery(id+"F5.imprint","IMPRINT",EDGE,{"derivedFrom":sQuery(id+"F5.wireOp",EDGE,"E201.MirrorCS")}),-1.0]])]});
            var Q11;
            Q11=makeQuery(id+"F5.imprint","IMPRINT",FACE,{"disambiguationData":[TD([[makeQuery(id+"F5.imprint","IMPRINT",EDGE,{"derivedFrom":sQuery(id+"F5.wireOp",EDGE,"E209.MirrorCS")}),1.0]])]});
            extrude(context, id + "F6", {"entities" : qUnion([Q0, Q1, Q2, Q3, Q4, Q5, Q6, Q7, Q8, Q9, Q10, Q11]), "operationType" : NewBodyOperationType.REMOVE, "oppositeDirection" : true, "depth" : 6 * mm});
        }
    });
